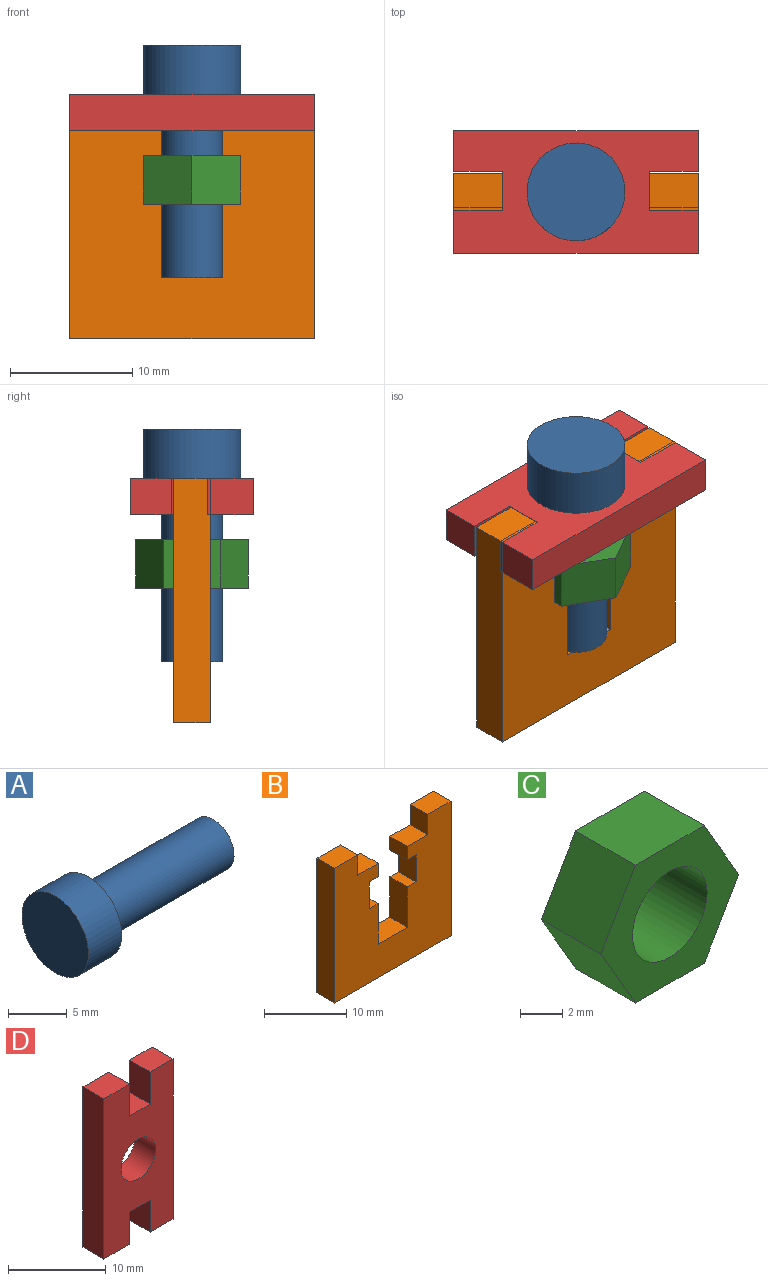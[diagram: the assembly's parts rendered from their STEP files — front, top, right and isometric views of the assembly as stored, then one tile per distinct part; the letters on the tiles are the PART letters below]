
ASSEMBLY  parts=4 mates=7
PART A: 5 faces, bbox 19x8x8 mm
  f0: plane 8x8mm, normal (-1,0,0), area 50.3mm2, adj f4
  f1: plane 5x5mm, normal (1,0,0), area 19.6mm2, adj f2
  f2: cylinder r=2.5mm len=15mm, axis (-1,0,0), area 235.6mm2, adj f1,f3
  f3: plane 8x8mm, normal (1,0,0), area 30.6mm2, adj f2,f4
  f4: cylinder r=4mm len=8mm, axis (-1,0,0), area 100.5mm2, adj f0,f3
PART B: 22 faces, bbox 20x3x20 mm
  f0: plane 3x3mm, normal (-1,0,0), area 9mm2, adj f1,f19,f20,f21
  f1: plane 3.5x3mm, normal (0,0,1), area 10.5mm2, adj f0,f2,f20,f21
  f2: plane 3x2mm, normal (-1,0,0), area 6mm2, adj f1,f3,f20,f21
  f3: plane 3x1.5mm, normal (0,0,-1), area 4.5mm2, adj f2,f4,f20,f21
  f4: plane 4x3mm, normal (-1,0,0), area 12mm2, adj f3,f5,f20,f21
  f5: plane 3x1.5mm, normal (0,0,1), area 4.5mm2, adj f4,f6,f20,f21
  f6: plane 6x3mm, normal (-1,0,0), area 18mm2, adj f5,f7,f20,f21
  f7: plane 5x3mm, normal (0,0,1), area 15mm2, adj f6,f8,f20,f21
  f8: plane 6x3mm, normal (1,0,0), area 18mm2, adj f7,f9,f20,f21
  f9: plane 3x1.5mm, normal (0,0,1), area 4.5mm2, adj f8,f10,f20,f21
  f10: plane 4x3mm, normal (1,0,0), area 12mm2, adj f9,f11,f20,f21
  f11: plane 3x1.5mm, normal (0,0,-1), area 4.5mm2, adj f10,f12,f20,f21
  f12: plane 3x2mm, normal (1,0,0), area 6mm2, adj f11,f13,f20,f21
  f13: plane 3.5x3mm, normal (0,0,1), area 10.5mm2, adj f12,f14,f20,f21
  f14: plane 3x3mm, normal (1,0,0), area 9mm2, adj f13,f15,f20,f21
  f15: plane 4x3mm, normal (0,0,1), area 12mm2, adj f14,f16,f20,f21
  f16: plane 20x3mm, normal (-1,0,0), area 60mm2, adj f15,f17,f20,f21
  f17: plane 20x3mm, normal (0,0,-1), area 60mm2, adj f16,f18,f20,f21
  f18: plane 20x3mm, normal (1,0,0), area 60mm2, adj f17,f19,f20,f21
  f19: plane 4x3mm, normal (0,0,1), area 12mm2, adj f0,f18,f20,f21
  f20: plane 20x20mm, normal (0,-1,0), area 292mm2, adj f0,f1,f2,f3,f4,f5,f6,f7
  f21: plane 20x20mm, normal (0,1,0), area 292mm2, adj f0,f1,f2,f3,f4,f5,f6,f7
PART C: 9 faces, bbox 9.2x4x8 mm
  f0: plane 4x4mm, normal (0.87,0,0.5), area 18.5mm2, adj f1,f6,f7,f8
  f1: plane 4.62x4mm, normal (0,0,1), area 18.5mm2, adj f0,f2,f7,f8
  f2: plane 4x4mm, normal (-0.87,0,0.5), area 18.5mm2, adj f1,f3,f7,f8
  f3: plane 4x4mm, normal (-0.87,0,-0.5), area 18.5mm2, adj f2,f4,f7,f8
  f4: plane 4.62x4mm, normal (0,0,-1), area 18.5mm2, adj f3,f6,f7,f8
  f5: cylinder r=2.5mm len=5mm, axis (0,1,0), area 62.8mm2, adj f7,f8
  f6: plane 4x4mm, normal (0.87,0,-0.5), area 18.5mm2, adj f0,f4,f7,f8
  f7: plane 9.24x8.01mm, normal (0,-1,0), area 35.8mm2, adj f0,f1,f2,f3,f4,f5,f6
  f8: plane 9.24x8.01mm, normal (0,1,0), area 35.8mm2, adj f0,f1,f2,f3,f4,f5,f6
PART D: 15 faces, bbox 10x3x20 mm
  f0: plane 4x3mm, normal (-1,0,0), area 12mm2, adj f1,f12,f13,f14
  f1: plane 3.29x3mm, normal (0,0,-1), area 9.9mm2, adj f0,f2,f13,f14
  f2: plane 20x3mm, normal (1,0,0), area 60mm2, adj f1,f3,f13,f14
  f3: plane 3.29x3mm, normal (0,0,1), area 9.9mm2, adj f2,f4,f13,f14
  f4: plane 4x3mm, normal (-1,0,0), area 12mm2, adj f3,f5,f13,f14
  f5: plane 3x3mm, normal (0,0,1), area 9mm2, adj f4,f6,f13,f14
  f6: plane 4x3mm, normal (1,0,0), area 12mm2, adj f5,f7,f13,f14
  f7: plane 3.71x3mm, normal (0,0,1), area 11.1mm2, adj f6,f8,f13,f14
  f8: plane 20x3mm, normal (-1,0,0), area 60mm2, adj f7,f9,f13,f14
  f9: plane 3.71x3mm, normal (0,0,-1), area 11.1mm2, adj f8,f10,f13,f14
  f10: plane 4x3mm, normal (1,0,0), area 12mm2, adj f9,f12,f13,f14
  f11: cylinder r=2.5mm len=5mm, axis (0,1,0), area 47.1mm2, adj f13,f14
  f12: plane 3x3mm, normal (0,0,-1), area 9mm2, adj f0,f10,f13,f14
  f13: plane 20x10mm, normal (0,-1,0), area 156.4mm2, adj f0,f1,f2,f3,f4,f5,f6,f7
  f14: plane 20x10mm, normal (0,1,0), area 156.4mm2, adj f0,f1,f2,f3,f4,f5,f6,f7
PLACE A rot(axis=(-0.71,0,0.71),180deg) t=(8.79,-19.02,9.03)mm
PLACE B t=(-33.73,-17.51,5.73)mm fixed
PLACE C rot(axis=(0.58,0.58,0.58),120deg) t=(-68.94,37.83,7.46)mm
PLACE D rot(axis=(-0.58,-0.58,0.58),120deg) t=(2.64,-53.31,9.46)mm
MATE cylindrical C.f5 <-> A.f2  axis (0,0,1) through (-33.5,-19.02,3.46)mm
MATE planar A.f2 <-> D.f13  axis (0,0,-1) through (-33.5,-19.02,12.46)mm
MATE planar D.f12 <-> B.f0  axis (1,0,0) through (-27.5,-18.81,10.96)mm
MATE planar C.f1 <-> B.f4  axis (1,0,0) through (-29.5,-19.02,5.46)mm
MATE cylindrical A.f2 <-> D.f11  axis (0,0,1) through (-33.5,-19.02,4.96)mm
MATE planar C.f5 <-> B.f9  axis (0,0,-1) through (-33.5,-19.02,3.46)mm
MATE planar D.f13 <-> B.f15  axis (0,0,1) through (-39.5,-20.31,12.46)mm
